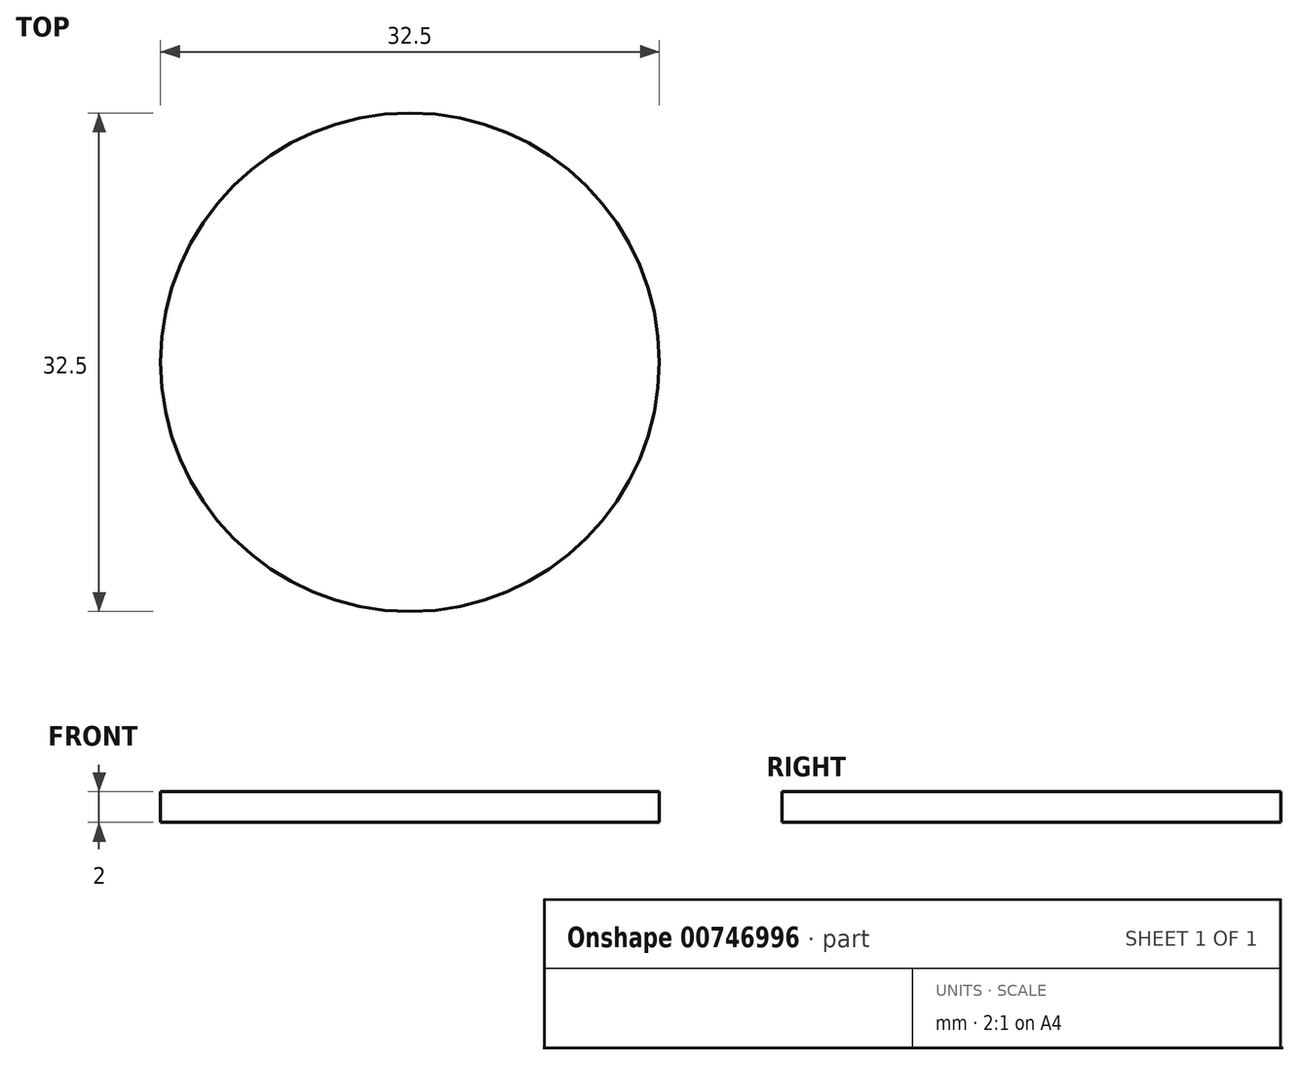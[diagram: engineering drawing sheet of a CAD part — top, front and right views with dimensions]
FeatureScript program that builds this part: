
annotation { "Feature Type Name" : "Feature", "Feature Type Description" : "" }
export const myFeature = defineFeature(function(context is Context, id is Id, definition is map)
    precondition{}
    {
        {
            var Q0;
            Q0=qCreatedBy(makeId("Top.planeOp"),FACE);
            var sketch = newSketch(context, id + "F0", { "sketchPlane" : qUnion([Q0])});
            skCircle(sketch, "E0", {"center": v(0, 0) * mm, "radius": 16.25 * mm});
            skSolve(sketch);
        }
        {
            var Q0;
            Q0=makeQuery(id+"F0.imprint","IMPRINT",FACE,{"disambiguationData":[TD([[makeQuery(id+"F0.imprint","IMPRINT",EDGE,{"derivedFrom":sQuery(id+"F0.wireOp",EDGE,"E0")}),1.0]])]});
            extrude(context, id + "F1", {"entities" : qUnion([Q0]), "depth" : 2 * mm, "offsetDistance" : 25 * mm});
        }
    });
